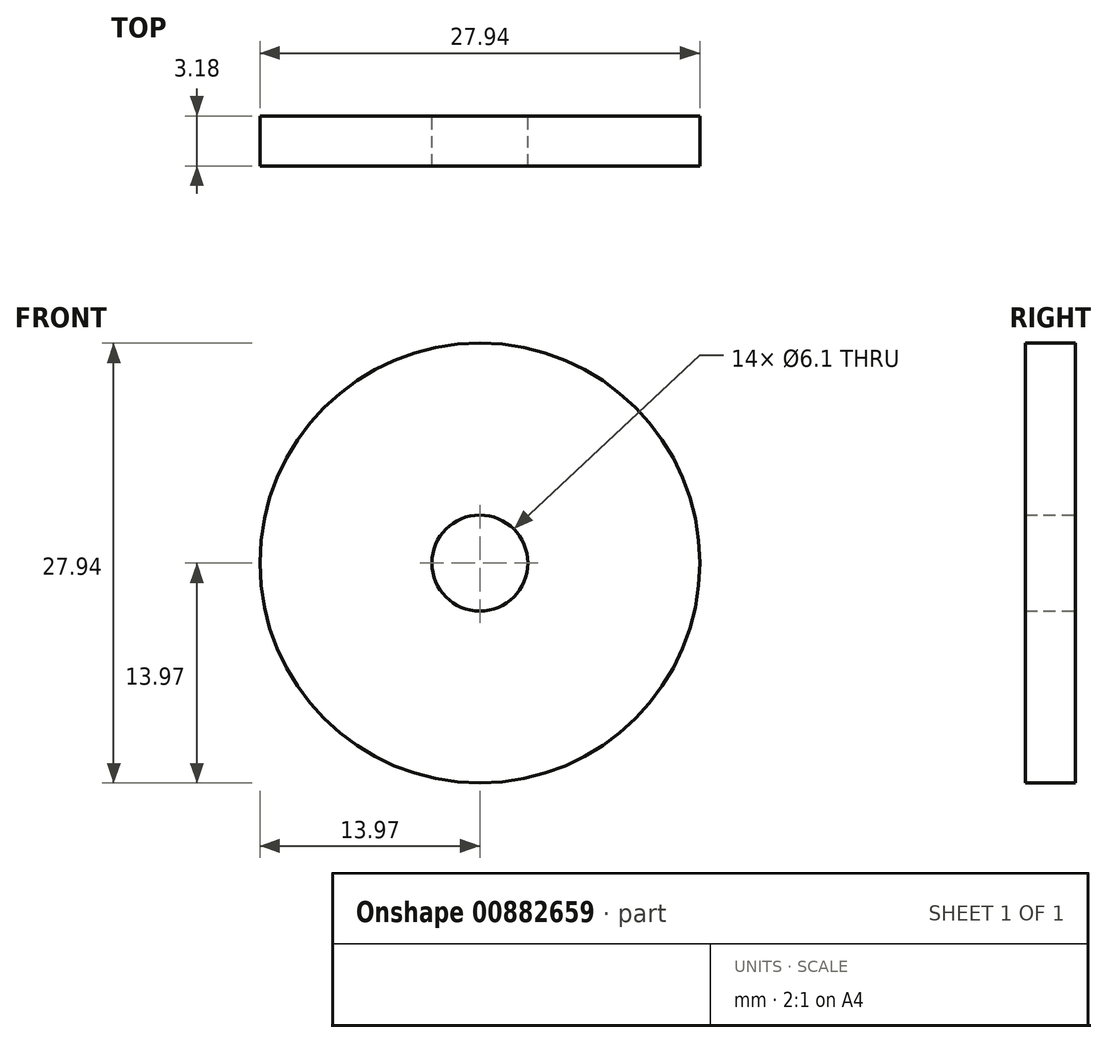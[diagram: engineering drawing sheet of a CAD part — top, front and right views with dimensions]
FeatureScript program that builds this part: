
annotation { "Feature Type Name" : "Feature", "Feature Type Description" : "" }
export const myFeature = defineFeature(function(context is Context, id is Id, definition is map)
    precondition{}
    {
        {
            var Q0;
            Q0=qCreatedBy(makeId("Front.planeOp"),FACE);
            var sketch = newSketch(context, id + "F0", { "sketchPlane" : qUnion([Q0])});
            skPoint(sketch, "E0.middle", {"position": v(0, 0) * mm});
            skCircle(sketch, "E1", {"center": v(0, 0) * mm, "radius": 3.05 * mm});
            skCircle(sketch, "E2", {"center": v(0, 0) * mm, "radius": 13.97 * mm});
            skSolve(sketch);
        }
        {
            var Q0;
            Q0=makeQuery(id+"F0.imprint","IMPRINT",FACE,{"disambiguationData":[TD([[makeQuery(id+"F0.imprint","IMPRINT",EDGE,{"derivedFrom":sQuery(id+"F0.wireOp",EDGE,"E1")}),-1.0]])]});
            extrude(context, id + "F1", {"entities" : qUnion([Q0]), "depth" : 3.17 * mm, "offsetDistance" : 25.4 * mm});
        }
    });
